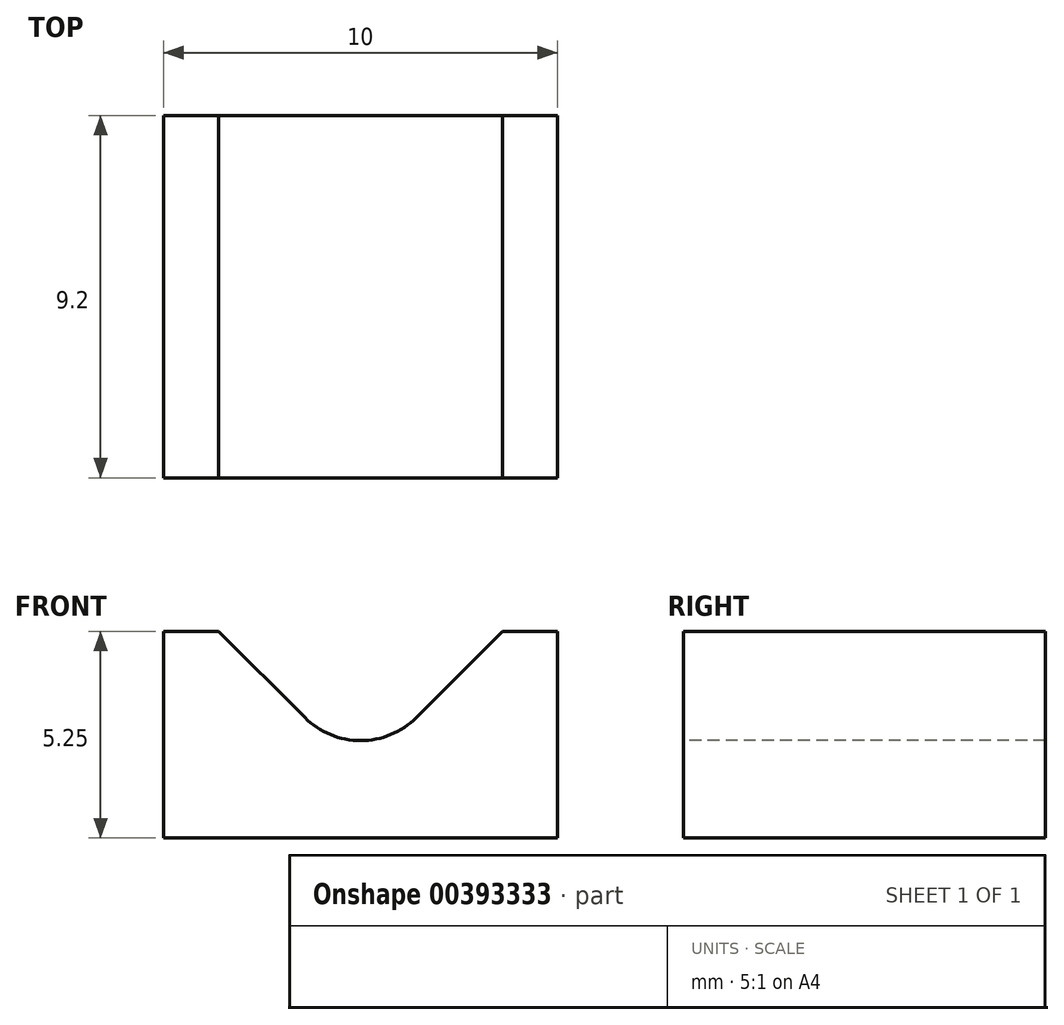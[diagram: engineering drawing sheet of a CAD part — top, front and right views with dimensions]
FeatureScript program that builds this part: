
annotation { "Feature Type Name" : "Feature", "Feature Type Description" : "" }
export const myFeature = defineFeature(function(context is Context, id is Id, definition is map)
    precondition{}
    {
        {
            var Q0;
            Q0=qCreatedBy(makeId("Front.planeOp"),FACE);
            var sketch = newSketch(context, id + "F0", { "sketchPlane" : qUnion([Q0])});
            skLineSegment(sketch, "E0.bottom", {"start": v(-43.13, -23.7) * mm, "end": v(-33.13, -23.7) * mm});
            skLineSegment(sketch, "E0.top", {"start": v(-43.13, -18.45) * mm, "end": v(-41.73, -18.45) * mm});
            skLineSegment(sketch, "E0.left", {"start": v(-43.13, -23.7) * mm, "end": v(-43.13, -18.45) * mm});
            skLineSegment(sketch, "E0.right", {"start": v(-33.13, -23.7) * mm, "end": v(-33.13, -18.45) * mm});
            skCircle(sketch, "E1", {"center": v(-38.13, -16.4) * mm, "radius": 4 * mm});
            skLineSegment(sketch, "E2", {"start": v(-35.3, -19.23) * mm, "end": v(-38.13, -22.06) * mm});
            skLineSegment(sketch, "E3", {"start": v(-40.95, -19.23) * mm, "end": v(-38.13, -22.06) * mm});
            skLineSegment(sketch, "E4", {"start": v(-40.95, -19.23) * mm, "end": v(-41.73, -18.45) * mm});
            skLineSegment(sketch, "E5", {"start": v(-35.3, -19.23) * mm, "end": v(-34.52, -18.45) * mm});
            skLineSegment(sketch, "E6.trimOffspring", {"start": v(-34.52, -18.45) * mm, "end": v(-33.13, -18.45) * mm});
            skPoint(sketch, "E7.start.orphan", {"position": v(-38.13, -23.7) * mm});
            skSolve(sketch);
        }
        {
            var Q0;
            Q0=makeQuery(id+"F0.imprint","IMPRINT",FACE,{"disambiguationData":[TD([[makeQuery(id+"F0.imprint","IMPRINT",EDGE,{"derivedFrom":sQuery(id+"F0.wireOp",EDGE,"E0.bottom")}),1.0]])]});
            extrude(context, id + "F1", {"entities" : qUnion([Q0]), "endBound" : BoundingType.SYMMETRIC, "depth" : 9.2 * mm});
        }
        {
            var Q0;
            Q0=makeQuery(id+"F1.opExtrude","SWEPT_EDGE",EDGE,{"disambiguationData":[OSD([sQuery(id+"F0.wireOp",EDGE,"E2"),sQuery(id+"F0.wireOp",EDGE,"E3")])]});
            fillet(context, id + "F2", {"entities" : qUnion([Q0]), "radius" : 2 * mm, "tangentPropagation" : true, "allowEdgeOverflow" : false});
        }
    });
